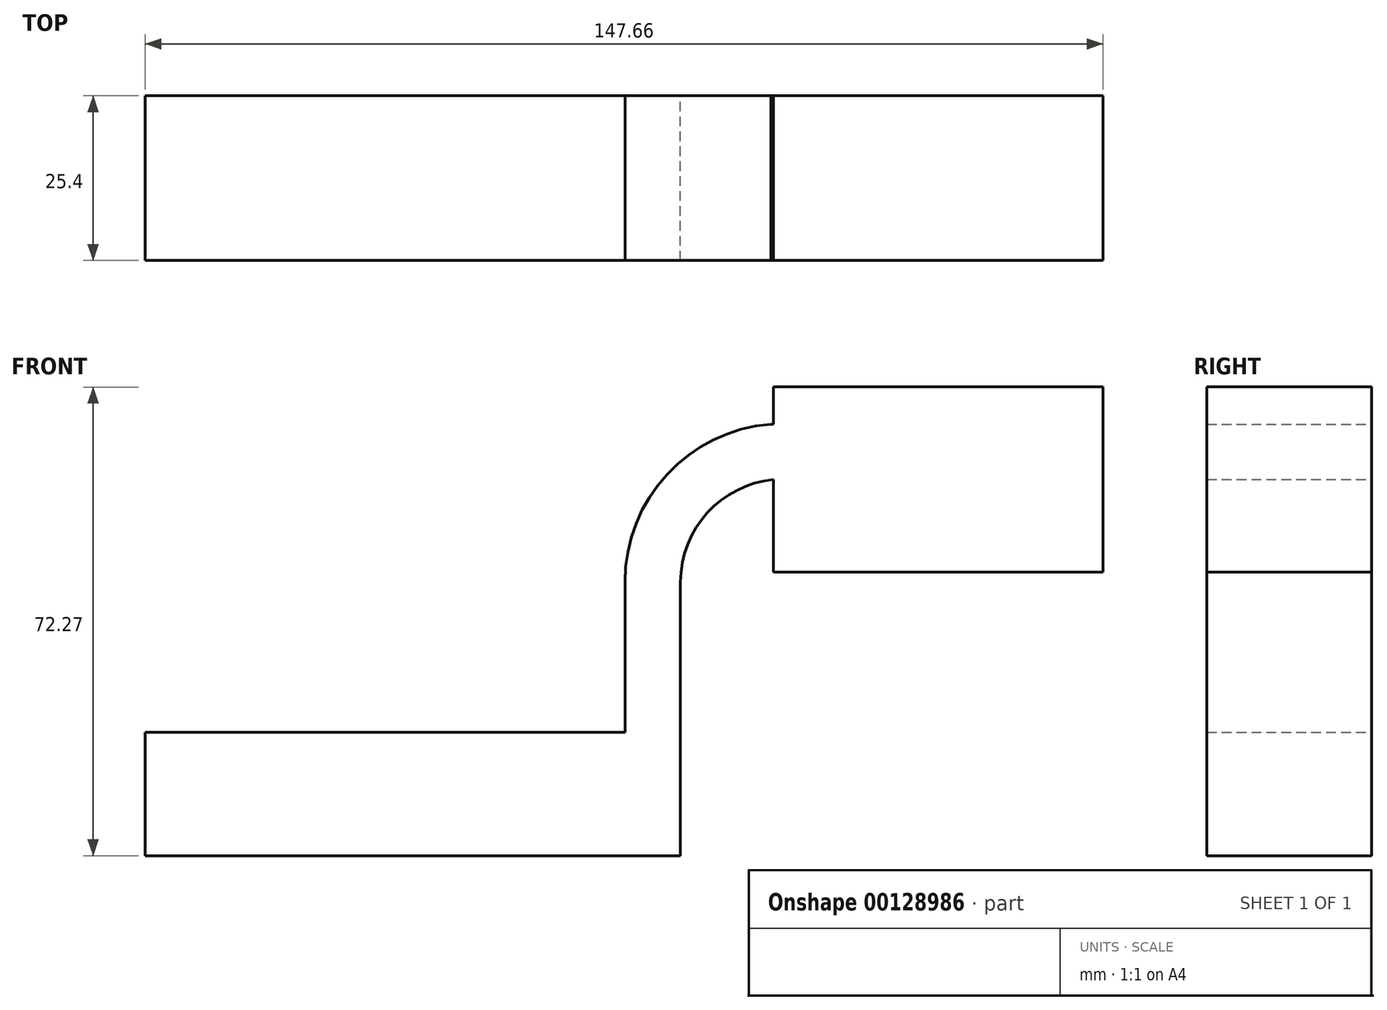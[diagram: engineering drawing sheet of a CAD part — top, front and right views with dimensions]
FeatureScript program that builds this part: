
annotation { "Feature Type Name" : "Feature", "Feature Type Description" : "" }
export const myFeature = defineFeature(function(context is Context, id is Id, definition is map)
    precondition{}
    {
        {
            var Q0;
            Q0=qCreatedBy(makeId("Front.planeOp"),FACE);
            var sketch = newSketch(context, id + "F0", { "sketchPlane" : qUnion([Q0])});
            skLineSegment(sketch, "E0.bottom", {"start": v(41.27, 9.53) * mm, "end": v(-41.28, 9.53) * mm});
            skLineSegment(sketch, "E0.top", {"start": v(41.28, -9.52) * mm, "end": v(-41.27, -9.52) * mm});
            skLineSegment(sketch, "E0.left", {"start": v(41.28, 9.53) * mm, "end": v(41.28, -9.52) * mm});
            skLineSegment(sketch, "E0.right", {"start": v(-41.28, 9.53) * mm, "end": v(-41.27, -9.52) * mm});
            skPoint(sketch, "E0.middle", {"position": v(0, 0) * mm});
            skLineSegment(sketch, "E1.bottom", {"start": v(106.39, 34.17) * mm, "end": v(55.59, 34.17) * mm});
            skLineSegment(sketch, "E1.top", {"start": v(106.39, 62.74) * mm, "end": v(55.59, 62.74) * mm});
            skLineSegment(sketch, "E1.left", {"start": v(106.39, 34.17) * mm, "end": v(106.39, 62.74) * mm});
            skLineSegment(sketch, "E1.right", {"start": v(55.59, 34.17) * mm, "end": v(55.59, 62.74) * mm});
            skPoint(sketch, "E1.middle", {"position": v(80.99, 48.45) * mm});
            skLineSegment(sketch, "E2", {"start": v(41.27, 9.53) * mm, "end": v(41.27, 32.66) * mm});
            skArc(sketch, "E3", {"start": v(41.27, 32.66) * mm, "mid": v(45.39, 43.32) * mm, "end": v(55.59, 48.45) * mm});
            skLineSegment(sketch, "E4", {"start": v(55.59, 48.45) * mm, "end": v(80.99, 48.45) * mm});
            skLineSegment(sketch, "E5.0", {"start": v(55.21, 57.02) * mm, "end": v(81.93, 57.02) * mm});
            skArc(sketch, "E5.1", {"start": v(32.7, 32.66) * mm, "mid": v(39.2, 49.24) * mm, "end": v(55.21, 57.02) * mm});
            skLineSegment(sketch, "E5.2", {"start": v(32.7, 9.53) * mm, "end": v(32.7, 32.66) * mm});
            skSolve(sketch);
        }
        {
            var Q0;
            {var subQ1=sQuery(id+"F0.wireOp",EDGE,"E1.bottom");Q0=makeQuery(id+"F0.imprint","IMPRINT",FACE,{"disambiguationData":[TD([[makeQuery(id+"F0.imprint","IMPRINT",EDGE,{"derivedFrom":subQ1}),-1.0]])]});}
            var Q1;
            {var subQ1=sQuery(id+"F0.wireOp",EDGE,"E2");Q1=makeQuery(id+"F0.imprint","IMPRINT",FACE,{"disambiguationData":[TD([[makeQuery(id+"F0.imprint","IMPRINT",EDGE,{"derivedFrom":subQ1}),1.0]])]});}
            var Q2;
            Q2=makeQuery(id+"F0.imprint","IMPRINT",FACE,{"disambiguationData":[TD([[makeQuery(id+"F0.imprint","IMPRINT",EDGE,{"derivedFrom":sQuery(id+"F0.wireOp",EDGE,"E0.top")}),-1.0]])]});
            extrude(context, id + "F1", {"entities" : qUnion([Q0, Q1, Q2]), "depth" : 25.4 * mm});
        }
    });
